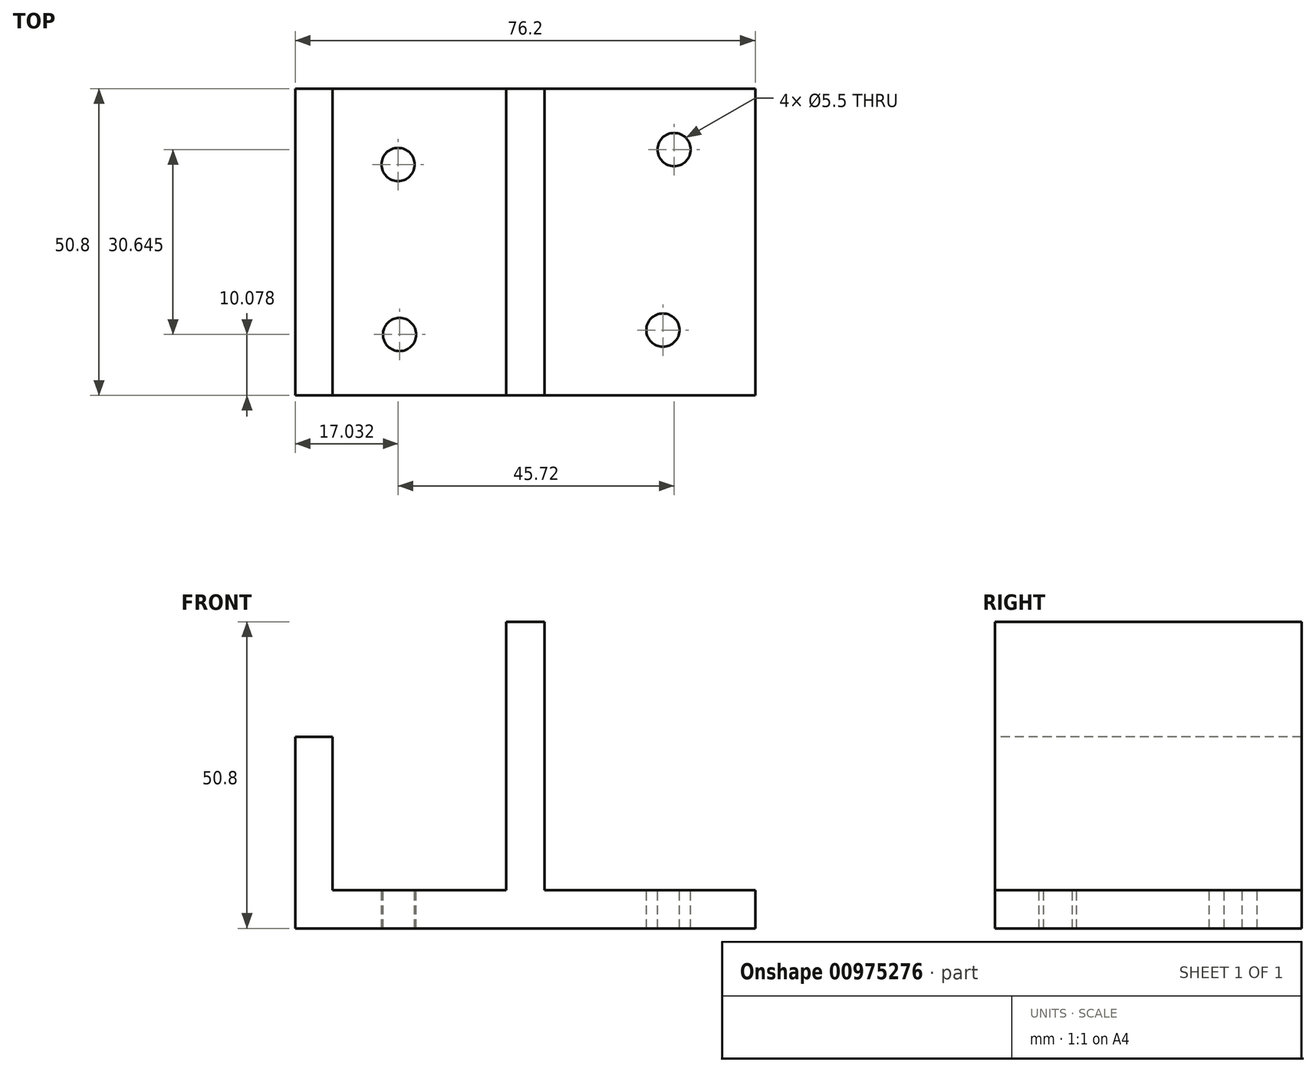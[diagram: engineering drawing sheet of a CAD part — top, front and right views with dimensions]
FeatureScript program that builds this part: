
annotation { "Feature Type Name" : "Feature", "Feature Type Description" : "" }
export const myFeature = defineFeature(function(context is Context, id is Id, definition is map)
    precondition{}
    {
        {
            var Q0;
            Q0=qCreatedBy(makeId("Top.planeOp"),FACE);
            var sketch = newSketch(context, id + "F0", { "sketchPlane" : qUnion([Q0])});
            skLineSegment(sketch, "E0.bottom", {"start": v(38.1, 25.4) * mm, "end": v(-38.1, 25.4) * mm});
            skLineSegment(sketch, "E0.top", {"start": v(38.1, -25.4) * mm, "end": v(-38.1, -25.4) * mm});
            skLineSegment(sketch, "E0.left", {"start": v(38.1, 25.4) * mm, "end": v(38.1, -25.4) * mm});
            skLineSegment(sketch, "E0.right", {"start": v(-38.1, 25.4) * mm, "end": v(-38.1, -25.4) * mm});
            skPoint(sketch, "E0.middle", {"position": v(0, 0) * mm});
            skSolve(sketch);
        }
        {
            var Q0;
            Q0 = qSketchRegion(id + "F0", true);
            extrude(context, id + "F1", {"entities" : qUnion([Q0]), "depth" : 6.35 * mm, "offsetDistance" : 25.4 * mm});
        }
        {
            var Q0;
            Q0=qCreatedBy(makeId("Top.planeOp"),FACE);
            var sketch = newSketch(context, id + "F2", { "sketchPlane" : qUnion([Q0])});
            skLineSegment(sketch, "E1.bottom", {"start": v(3.18, 25.4) * mm, "end": v(-3.18, 25.4) * mm});
            skLineSegment(sketch, "E1.top", {"start": v(3.18, -25.4) * mm, "end": v(-3.18, -25.4) * mm});
            skLineSegment(sketch, "E1.left", {"start": v(3.18, 25.4) * mm, "end": v(3.18, -25.4) * mm});
            skLineSegment(sketch, "E1.right", {"start": v(-3.18, 25.4) * mm, "end": v(-3.18, -25.4) * mm});
            skPoint(sketch, "E1.middle", {"position": v(0, 0) * mm});
            skSolve(sketch);
        }
        {
            var Q0;
            Q0 = qSketchRegion(id + "F2", true);
            extrude(context, id + "F3", {"entities" : qUnion([Q0]), "operationType" : NewBodyOperationType.ADD, "depth" : 50.8 * mm, "offsetDistance" : 25.4 * mm});
        }
        {
            var Q0;
            {var subQ0=sQuery(id+"F0.wireOp",EDGE,"E0.top");var subQ1=sQuery(id+"F0.wireOp",EDGE,"E0.right");var subQ2=sQuery(id+"F0.wireOp",EDGE,"E0.bottom");Q0=makeQuery(id+"F3.boolean.opBoolean","SPLIT",FACE,{"disambiguationData":[TD([makeQuery(id+"F1.opExtrude","SWEPT_FACE",FACE,{"disambiguationData":[OSD([subQ1])]})])],"derivedFrom":makeQuery(id+"F1.opExtrude","CAP_FACE",FACE,{"disambiguationData":[OSD([subQ2,subQ0,sQuery(id+"F0.wireOp",EDGE,"E0.left"),subQ1])],"isStart":false})});}
            var sketch = newSketch(context, id + "F4", { "sketchPlane" : qUnion([Q0])});
            skPoint(sketch, "E2", {"position": v(-21.07, 12.85) * mm});
            skPoint(sketch, "E3", {"position": v(-20.82, -15.32) * mm});
            skPoint(sketch, "E4", {"position": v(22.8, -14.58) * mm});
            skPoint(sketch, "E5", {"position": v(24.65, 15.32) * mm});
            skSolve(sketch);
        }
        {
            var Q0;
            Q0=sQuery(id+"F4.wireOp",VERTEX,"E2");
            var Q1;
            Q1=sQuery(id+"F4.wireOp",VERTEX,"E3");
            var Q2;
            Q2=sQuery(id+"F4.wireOp",VERTEX,"E4");
            var Q3;
            Q3=sQuery(id+"F4.wireOp",VERTEX,"E5");
            var Q4;
            Q4=makeQuery(id+"F1.opExtrude","SWEPT_BODY",BODY,{"disambiguationData":[OSD([sQuery(id+"F0.wireOp",EDGE,"E0.bottom"),sQuery(id+"F0.wireOp",EDGE,"E0.top"),sQuery(id+"F0.wireOp",EDGE,"E0.left"),sQuery(id+"F0.wireOp",EDGE,"E0.right")])]});
            hole(context, id + "F5", {"style" : HoleStyle.SIMPLE, "endStyle" : HoleEndStyle.THROUGH, "standardTappedOrClearance" : lookupTablePath({ "fit" : "Normal", "standard" : "ISO", "size" : "M5", "type" : "Clearance" }), "standardBlindInLast" : lookupTablePath({ "fit" : "Normal", "standard" : "ISO", "engagement" : "75%", "pitch" : "0.8 mm", "size" : "M5", "type" : "Clearance & tapped" }), "holeDiameter" : 5.5 * mm, "majorDiameter" : 6.35 * mm, "isTappedThrough" : true, "tappedDepth" : 12.7 * mm, "tapClearance" : 3, "locations" : qUnion([Q0, Q1, Q2, Q3]), "scope" : qUnion([Q4])});
        }
        {
            var Q0;
            {var subQ0=sQuery(id+"F0.wireOp",EDGE,"E0.top");var subQ1=sQuery(id+"F0.wireOp",EDGE,"E0.right");var subQ2=sQuery(id+"F0.wireOp",EDGE,"E0.bottom");Q0=makeQuery(id+"F3.boolean.opBoolean","SPLIT",FACE,{"disambiguationData":[TD([makeQuery(id+"F1.opExtrude","SWEPT_FACE",FACE,{"disambiguationData":[OSD([subQ1])]})])],"derivedFrom":makeQuery(id+"F1.opExtrude","CAP_FACE",FACE,{"disambiguationData":[OSD([subQ2,subQ0,sQuery(id+"F0.wireOp",EDGE,"E0.left"),subQ1])],"isStart":false})});}
            var sketch = newSketch(context, id + "F6", { "sketchPlane" : qUnion([Q0])});
            skLineSegment(sketch, "E6.bottom", {"start": v(-38.1, 25.4) * mm, "end": v(-31.94, 25.4) * mm});
            skLineSegment(sketch, "E6.top", {"start": v(-38.1, -25.4) * mm, "end": v(-31.94, -25.4) * mm});
            skLineSegment(sketch, "E6.left", {"start": v(-38.1, 25.4) * mm, "end": v(-38.1, -25.4) * mm});
            skLineSegment(sketch, "E6.right", {"start": v(-31.94, 25.4) * mm, "end": v(-31.94, -25.4) * mm});
            skSolve(sketch);
        }
        {
            var Q0;
            Q0 = qSketchRegion(id + "F6", true);
            extrude(context, id + "F7", {"entities" : qUnion([Q0]), "operationType" : NewBodyOperationType.ADD, "depth" : 25.4 * mm, "offsetDistance" : 25.4 * mm});
        }
    });
